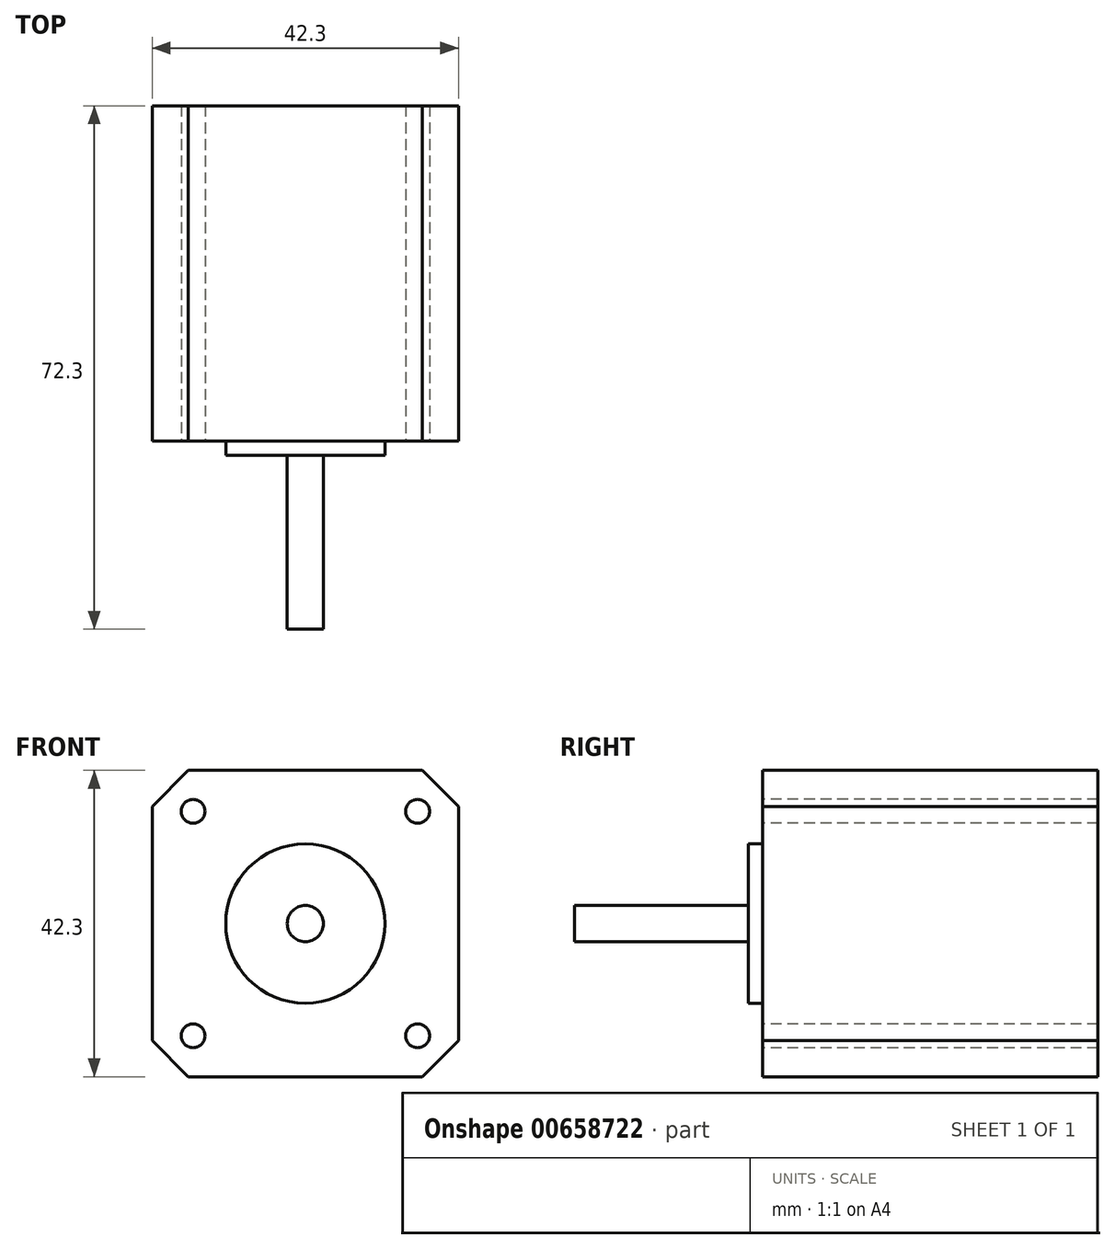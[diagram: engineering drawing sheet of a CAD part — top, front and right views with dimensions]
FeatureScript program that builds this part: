
annotation { "Feature Type Name" : "Feature", "Feature Type Description" : "" }
export const myFeature = defineFeature(function(context is Context, id is Id, definition is map)
    precondition{}
    {
        {
            var Q0;
            Q0=qCreatedBy(makeId("Front.planeOp"),FACE);
            var sketch = newSketch(context, id + "F0", { "sketchPlane" : qUnion([Q0])});
            skLineSegment(sketch, "E0.bottom", {"start": v(21.15, 21.15) * mm, "end": v(-21.15, 21.15) * mm});
            skLineSegment(sketch, "E0.top", {"start": v(21.15, -21.15) * mm, "end": v(-21.15, -21.15) * mm});
            skLineSegment(sketch, "E0.left", {"start": v(21.15, 21.15) * mm, "end": v(21.15, -21.15) * mm});
            skLineSegment(sketch, "E0.right", {"start": v(-21.15, 21.15) * mm, "end": v(-21.15, -21.15) * mm});
            skPoint(sketch, "E0.middle", {"position": v(0, 0) * mm});
            skSolve(sketch);
        }
        {
            var Q0;
            Q0 = qSketchRegion(id + "F0", true);
            extrude(context, id + "F1", {"entities" : qUnion([Q0]), "oppositeDirection" : true, "depth" : 46.3 * mm, "offsetDistance" : 25 * mm});
        }
        {
            var Q0;
            Q0=makeQuery(id+"F1.opExtrude","SWEPT_EDGE",EDGE,{"disambiguationData":[OSD([sQuery(id+"F0.wireOp",EDGE,"E0.bottom"),sQuery(id+"F0.wireOp",EDGE,"E0.right")])]});
            var Q1;
            Q1=makeQuery(id+"F1.opExtrude","SWEPT_EDGE",EDGE,{"disambiguationData":[OSD([sQuery(id+"F0.wireOp",EDGE,"E0.bottom"),sQuery(id+"F0.wireOp",EDGE,"E0.left")])]});
            var Q2;
            Q2=makeQuery(id+"F1.opExtrude","SWEPT_EDGE",EDGE,{"disambiguationData":[OSD([sQuery(id+"F0.wireOp",EDGE,"E0.top"),sQuery(id+"F0.wireOp",EDGE,"E0.right")])]});
            var Q3;
            Q3=makeQuery(id+"F1.opExtrude","SWEPT_EDGE",EDGE,{"disambiguationData":[OSD([sQuery(id+"F0.wireOp",EDGE,"E0.top"),sQuery(id+"F0.wireOp",EDGE,"E0.left")])]});
            chamfer(context, id + "F2", {"entities" : qUnion([Q0, Q1, Q2, Q3]), "width" : 5 * mm, "tangentPropagation" : true});
        }
        {
            var Q0;
            Q0=makeQuery(id+"F1.opExtrude","CAP_FACE",FACE,{"disambiguationData":[OSD([sQuery(id+"F0.wireOp",EDGE,"E0.bottom"),sQuery(id+"F0.wireOp",EDGE,"E0.top"),sQuery(id+"F0.wireOp",EDGE,"E0.left"),sQuery(id+"F0.wireOp",EDGE,"E0.right")])],"isStart":true});
            var sketch = newSketch(context, id + "F3", { "sketchPlane" : qUnion([Q0])});
            skCircle(sketch, "E1", {"center": v(0, 0) * mm, "radius": 11 * mm});
            skSolve(sketch);
        }
        {
            var Q0;
            Q0 = qSketchRegion(id + "F3", true);
            extrude(context, id + "F4", {"entities" : qUnion([Q0]), "operationType" : NewBodyOperationType.ADD, "depth" : 2 * mm, "offsetDistance" : 25 * mm});
        }
        {
            var Q0;
            Q0=makeQuery(id+"F4.opExtrude","CAP_FACE",FACE,{"disambiguationData":[OSD([sQuery(id+"F3.wireOp",EDGE,"E1")])],"isStart":false});
            var sketch = newSketch(context, id + "F5", { "sketchPlane" : qUnion([Q0])});
            skCircle(sketch, "E2", {"center": v(0, 0) * mm, "radius": 2.5 * mm});
            skSolve(sketch);
        }
        {
            var Q0;
            Q0 = qSketchRegion(id + "F5", true);
            extrude(context, id + "F6", {"entities" : qUnion([Q0]), "operationType" : NewBodyOperationType.ADD, "depth" : 24 * mm, "offsetDistance" : 25 * mm});
        }
        {
            var Q0;
            Q0=makeQuery(id+"F1.opExtrude","CAP_FACE",FACE,{"disambiguationData":[OSD([sQuery(id+"F0.wireOp",EDGE,"E0.bottom"),sQuery(id+"F0.wireOp",EDGE,"E0.top"),sQuery(id+"F0.wireOp",EDGE,"E0.left"),sQuery(id+"F0.wireOp",EDGE,"E0.right")])],"isStart":true});
            var sketch = newSketch(context, id + "F7", { "sketchPlane" : qUnion([Q0])});
            skPoint(sketch, "E3", {"position": v(-15.5, 15.5) * mm});
            skPoint(sketch, "E4", {"position": v(15.5, 15.5) * mm});
            skPoint(sketch, "E5", {"position": v(15.5, -15.5) * mm});
            skPoint(sketch, "E6", {"position": v(-15.5, -15.5) * mm});
            skLineSegment(sketch, "E7.bottom", {"start": v(15.5, 15.5) * mm, "end": v(-15.5, 15.5) * mm, "construction": true});
            skLineSegment(sketch, "E7.top", {"start": v(15.5, -15.5) * mm, "end": v(-15.5, -15.5) * mm, "construction": true});
            skLineSegment(sketch, "E7.left", {"start": v(15.5, 15.5) * mm, "end": v(15.5, -15.5) * mm, "construction": true});
            skLineSegment(sketch, "E7.right", {"start": v(-15.5, 15.5) * mm, "end": v(-15.5, -15.5) * mm, "construction": true});
            skLineSegment(sketch, "E8", {"start": v(0, 15.5) * mm, "end": v(0, -15.5) * mm, "construction": true});
            skSolve(sketch);
        }
        {
            var Q0;
            Q0=sQuery(id+"F7.wireOp",VERTEX,"E4");
            var Q1;
            Q1=sQuery(id+"F7.wireOp",VERTEX,"E3");
            var Q2;
            Q2=sQuery(id+"F7.wireOp",VERTEX,"E6");
            var Q3;
            Q3=sQuery(id+"F7.wireOp",VERTEX,"E5");
            var Q4;
            Q4=makeQuery(id+"F1.opExtrude","SWEPT_BODY",BODY,{"disambiguationData":[OSD([sQuery(id+"F0.wireOp",EDGE,"E0.bottom"),sQuery(id+"F0.wireOp",EDGE,"E0.top"),sQuery(id+"F0.wireOp",EDGE,"E0.left"),sQuery(id+"F0.wireOp",EDGE,"E0.right")])]});
            hole(context, id + "F8", {"style" : HoleStyle.SIMPLE, "endStyle" : HoleEndStyle.THROUGH, "standardTappedOrClearance" : lookupTablePath({ "standard" : "ISO", "fit" : "Normal", "size" : "M3", "type" : "Clearance" }), "standardBlindInLast" : lookupTablePath({ "fit" : "Standard", "standard" : "ISO", "size" : "M3", "type" : "Clearance" }), "holeDiameter" : 3.3 * mm, "majorDiameter" : 5 * mm, "isTappedThrough" : true, "tappedDepth" : 12 * mm, "tapClearance" : 3, "locations" : qUnion([Q0, Q1, Q2, Q3]), "scope" : qUnion([Q4])});
        }
    });
